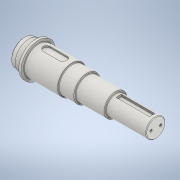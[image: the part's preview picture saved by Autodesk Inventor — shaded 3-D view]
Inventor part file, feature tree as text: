
AUTODESK INVENTOR PART (.ipt)
format: ipt  version: 2020 (Build 240168000, 168)  size: 266,752 bytes
history: native  units: mm
features: sketch x6, extrude x4, plane x2, other x2, projected_geometry x2, revolve x1, chamfer x1, fillet x1, hole x1
ambient origin geometry x6: Origin, XZ Plane, XY Plane, X Axis, Y Axis, Z Axis
bodies: 实体1 (feature_tree)
feature tree (20):
  revolve  "旋转1"  [1 undecoded]
  extrude  "拉伸4"  Depth=144.0mm
  extrude  "拉伸5"  Depth=110.0mm
  chamfer  "倒角1"  Distance=19.0mm
  fillet  "圆角1"  Radius=30.0mm
  sketch  "草图8"  dims[d6=120.0mm d7=110.0mm]
  hole  "孔1"  [1 undecoded]
  plane  "工作平面1"
  extrude  "拉伸6"  Depth=32.0mm
  plane  "工作平面2"
  extrude  "拉伸7"  Depth=32.0mm
  other  "起始平面"
  other  "主草图"
  sketch  "草图6"  dims[d0=0.0mm d1=0.0mm d2=0.0mm d3=110.0mm]
  projected_geometry  "投影回路3"
  sketch  "草图7"  dims[d4=116.0mm d5=144.0mm]
  projected_geometry  "投影回路4"
  sketch  "草图9"  dims[d8=96.0mm]
  sketch  "草图10"  dims[d9=80.0mm]
  sketch  "草图11"  dims[d10=0.0mm d20=19.0mm d21=0.0mm d22=30.0mm d23=0.0mm d24=2.5mm d25=2.0mm d26=45.0deg d27=2.0mm d28=40.0mm d29=10.106mm d30=20.0mm d31=4.0mm d32=2.0mm d33=90.0deg d34=25.0mm d35=20.594885mm d36=140.0mm d37=22.0mm d38=14.0mm d39=9.0mm d40=0.0mm d41=100.0mm d42=32.0mm d43=36.0mm d44=7.0mm d45=0.0mm]
note: 2 required parameter values undecoded (feature->parameter linkage not recoverable at this tier; creation-order binding heuristic only, values carry confidence <= 0.55)